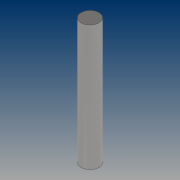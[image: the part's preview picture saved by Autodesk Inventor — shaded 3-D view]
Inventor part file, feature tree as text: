
AUTODESK INVENTOR PART (.ipt)
format: ipt  version: 2021 (Build 250183000, 183)  size: 75,776 bytes
history: native  units: mm
features: extrude x1, sketch x1
ambient origin geometry x8: Origin, YZ Plane, XZ Plane, XY Plane, X Axis, Y Axis, Z Axis, Center Point
bodies: Solid1 (feature_tree)
feature tree (2):
  extrude  "Extrusion1"  Depth=70.0mm TaperAngle=0.0deg
  sketch  "Sketch1"  dims[d0=10.0mm d1=70.0mm d2=0.0mm]
